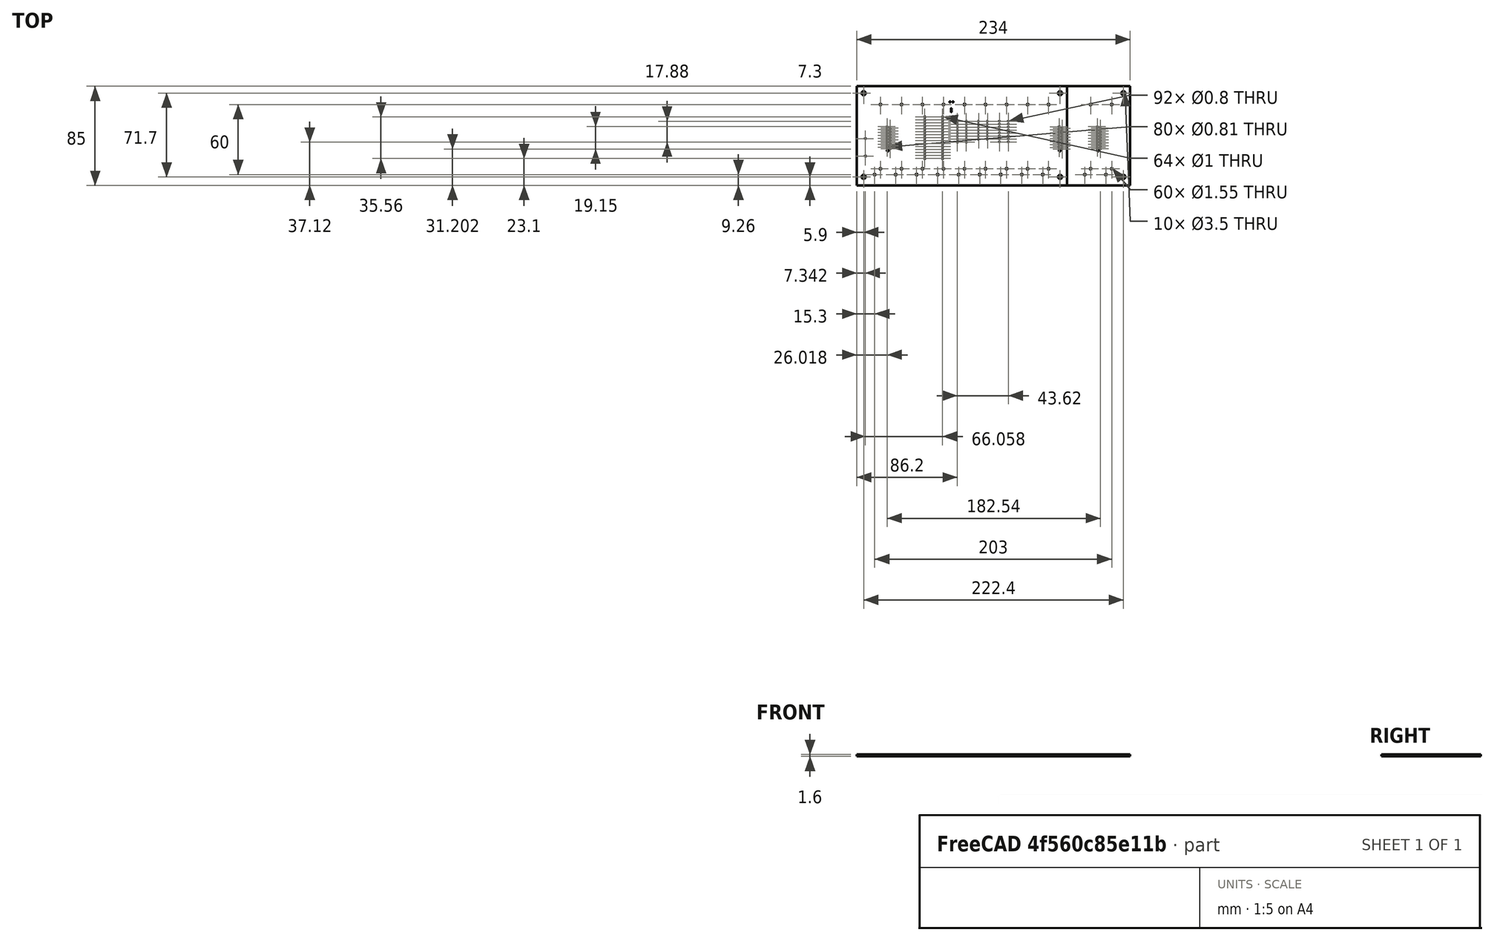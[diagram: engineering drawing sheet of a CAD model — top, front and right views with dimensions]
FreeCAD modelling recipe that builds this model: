
FCSTD DOCUMENT  (FreeCAD 0.20R29603 (Git))
Label: drawbars_pcb_small
License: All rights reserved
LicenseURL: http://en.wikipedia.org/wiki/All_rights_reserved
objects: App::Part×3, PartDesign::CoordinateSystem×1, Part::Feature×1, Sketcher::SketchObject×1, Part::Box×1, Part::Cut×1
note: 5 computed .brp shape members not serialized (recipe doc carries the construction recipe); baked Part::Feature solids carry a one-line shape summary decoded from their .brp

FEATURE [PartDesign::CoordinateSystem] Local_CS_3e93
  AttacherType = Attacher::AttachEngine3D
FEATURE [Part::Feature] Pcb_3e93
  Placement = pos=(-31.1,42.1,0) rot=(0,0,1;0rad)
  shape: bbox 234 x 85 x 1.6 mm, 179 faces (baked)
FEATURE [Sketcher::SketchObject] PCB_Sketch_3e93
  FullyConstrained = false
  sketch-geometry (4):
    g0: LineSegment StartX=-0.1 StartY=-84.9 StartZ=0 EndX=-0.1 EndY=0.1 EndZ=0
    g1: LineSegment StartX=-0.1 StartY=0.1 StartZ=0 EndX=233.9 EndY=0.1 EndZ=0
    g2: LineSegment StartX=233.9 StartY=-84.9 StartZ=0 EndX=-0.1 EndY=-84.9 EndZ=0
    g3: LineSegment StartX=233.9 StartY=-84.9 StartZ=0 EndX=233.9 EndY=0.1 EndZ=0
  constraints (4):
    c: Coincident(g0,g2)
    c: Coincident(g0,g1)
    c: Coincident(g2,g3)
    c: Coincident(g1,g3)
FEATURE [App::Part] Board_Geoms_3e93
  Group = -> [Local_CS_3e93,Pcb_3e93,PCB_Sketch_3e93]
  Origin = -> Origin
FEATURE [App::Part] Step_Models_3e93
  Origin = -> Origin002
FEATURE [App::Part] Board_3e93  label="drawbars"
  Group = -> [Board_Geoms_3e93,Step_Models_3e93]
  Origin = -> Origin001
FEATURE [Part::Box] Box  label="Cube"
  AttacherType = Attacher::AttachEngine3D
  Height = 10
  Length = 60
  Placement = pos=(180,-93,-6) rot=(0,0,1;0rad)
  Width = 100
FEATURE [Part::Cut] Cut
  Base = -> Board_3e93
  Tool = -> Box
